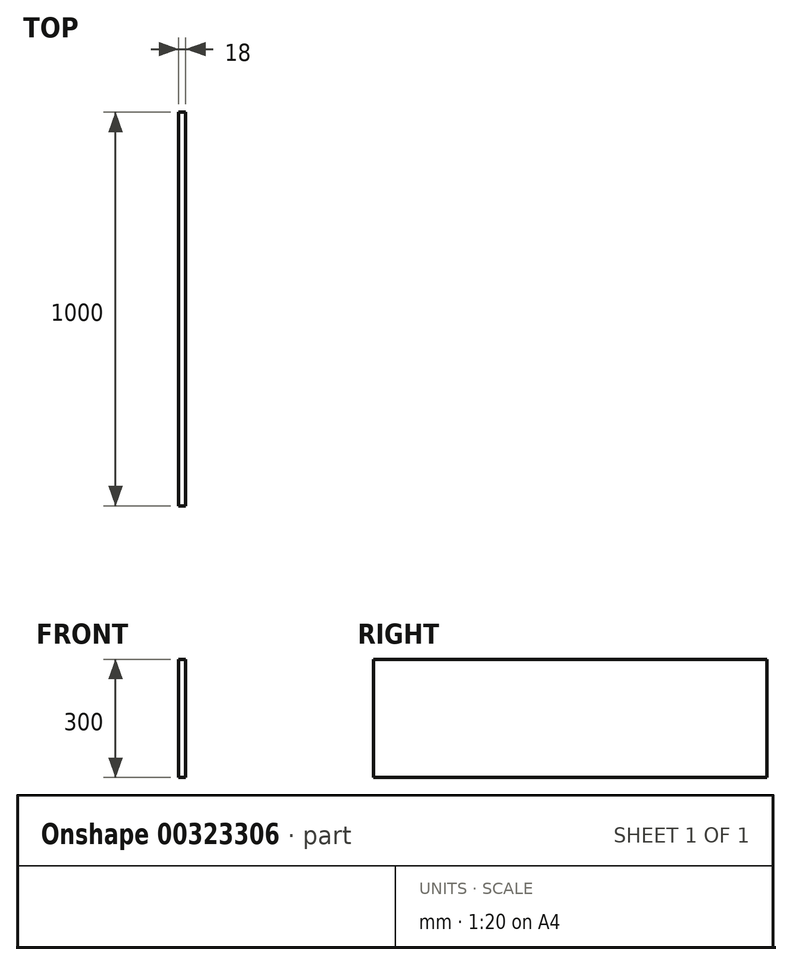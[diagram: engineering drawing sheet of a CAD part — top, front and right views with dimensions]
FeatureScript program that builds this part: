
annotation { "Feature Type Name" : "Feature", "Feature Type Description" : "" }
export const myFeature = defineFeature(function(context is Context, id is Id, definition is map)
    precondition{}
    {
        {
            var Q0;
            Q0=qCreatedBy(makeId("Right.planeOp"),FACE);
            var sketch = newSketch(context, id + "F0", { "sketchPlane" : qUnion([Q0])});
            skLineSegment(sketch, "E0.bottom", {"start": v(0, 0) * mm, "end": v(1000, 0) * mm});
            skLineSegment(sketch, "E0.top", {"start": v(0, 300) * mm, "end": v(1000, 300) * mm});
            skLineSegment(sketch, "E0.left", {"start": v(0, 0) * mm, "end": v(0, 300) * mm});
            skLineSegment(sketch, "E0.right", {"start": v(1000, 0) * mm, "end": v(1000, 300) * mm});
            skSolve(sketch);
        }
        {
            var Q0;
            Q0 = qSketchRegion(id + "F0", true);
            extrude(context, id + "F1", {"entities" : qUnion([Q0]), "depth" : 18 * mm, "offsetDistance" : 25 * mm});
        }
    });
